# Revit family: led_e_t5_batten_600_9w_800lm_3000k_ct_140043898
name_source: partatom
category: Leuchten
revit_build: Autodesk Revit 2016 (Build: 20190508_0715(x64)
units: mm (PartAtom-declared; Revit-internal decimal feet)

## family parameters
Basisbauteil = Fläche
Beim Laden mit Abzugskörper schneiden = Nein
Bemaßung runder Anschluss = Durchmesser verwenden
Gemeinsam genutzt = Nein
Lichtquelle = Nein
Raumberechnungspunkt = Nein
Teiletyp = Normal

## types (1)
- LED E T5 batten 600 9W 800lm 3000K CT (1 x LED, 900 lm)
    Approval mark = CE
    Beschreibung = Linear LED batten. Uniform, diffused light, creating a pleasant atmosphere. Trailing edge dimmable. Up to 50% lower energy consumption. Battens connect up to 15 meters. Including power cable, mounting and connection pieces (fixed and flexible). With transparant end caps. Free to position stainless steel mounting clips.
    CIE Flux Codes = 38 67 87 86 100
    Control Gear = Electronic ballast
    Height = 35 mm
    Hersteller = OPPLE
    Lamp Light Flux = 900 lm
    Lamp count = 1
    Lampe = 1 x LED
    Length = 600 mm
    Luminous efficacy = 100 lm/W
    ModVariant = Nein
    Modell = 140043898
    Mounting Place = Wall
    Mounting Type = Surface mounted
    Number of Poles = 1
    OnlyDefault = Ja
    Power Factor = 1
    Product Name = LED E T5 batten 600 9W 800lm 3000K CT
    Product group = T5 Batten EcoMax
    ProductGroupID = 2010
    Protection Class = Protection class I
    Protection Degree = IP 20
    RLX_Detail_Level = 1
    RlxData = <blob elided: 29549 chars, md5=cc49161e>
    Scheinlast = 9 VA
    Socket = socket
    Standby Power = 0 W
    System Light Flux = 900 lm
    System Power = 9 W
    Typenbild = 140043898.jpg
    Typenkommentare = Product without accessories
    URL = http://relux.com
    VarID = ---
    Voltage = 0 V
    Vorgabe-Ansicht = 1800 mm
    Weight = 0.00 kg
    Width = 22 mm

## geometry (parser evidence)
native form markers: Blend x4, Sweep x11
no freeform markers — native parametric forms only
